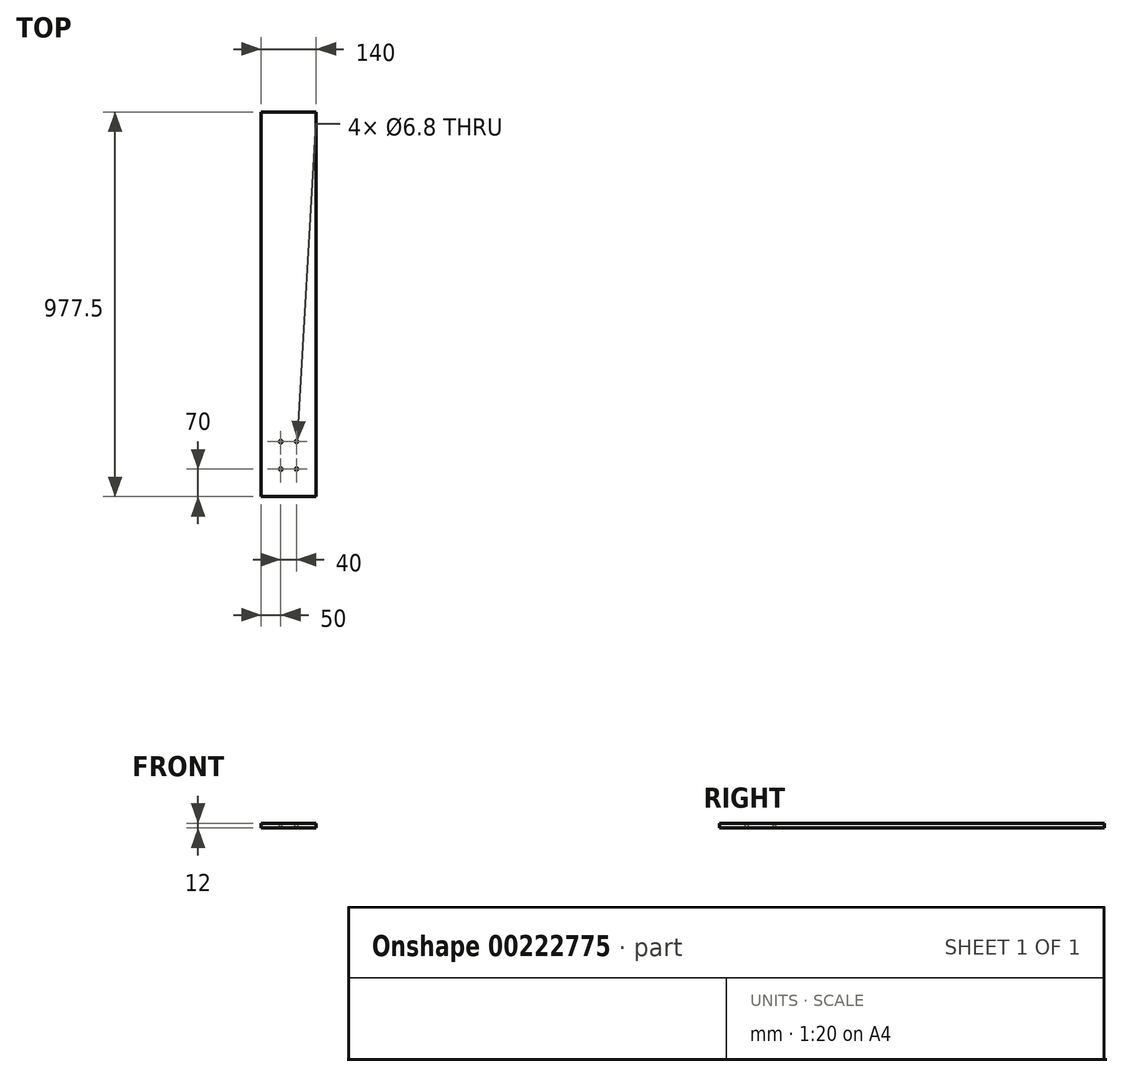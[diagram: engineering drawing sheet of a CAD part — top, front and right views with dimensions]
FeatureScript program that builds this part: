
annotation { "Feature Type Name" : "Feature", "Feature Type Description" : "" }
export const myFeature = defineFeature(function(context is Context, id is Id, definition is map)
    precondition{}
    {
        {
            var Q0;
            Q0=qCreatedBy(makeId("Top.planeOp"),FACE);
            var sketch = newSketch(context, id + "F0", { "sketchPlane" : qUnion([Q0])});
            skLineSegment(sketch, "E0.bottom", {"start": v(0, 0) * mm, "end": v(140, 0) * mm});
            skLineSegment(sketch, "E0.top", {"start": v(0, 977.5) * mm, "end": v(140, 977.5) * mm});
            skLineSegment(sketch, "E0.left", {"start": v(0, 0) * mm, "end": v(0, 977.5) * mm});
            skLineSegment(sketch, "E0.right", {"start": v(140, 0) * mm, "end": v(140, 977.5) * mm});
            skSolve(sketch);
        }
        {
            var Q0;
            Q0 = qSketchRegion(id + "F0", true);
            extrude(context, id + "F1", {"entities" : qUnion([Q0]), "depth" : 12 * mm});
        }
        {
            var Q0;
            Q0=makeQuery(id+"F1.opExtrude","CAP_FACE",FACE,{"disambiguationData":[OSD([sQuery(id+"F0.wireOp",EDGE,"E0.bottom"),sQuery(id+"F0.wireOp",EDGE,"E0.top"),sQuery(id+"F0.wireOp",EDGE,"E0.left"),sQuery(id+"F0.wireOp",EDGE,"E0.right")])],"isStart":false});
            var sketch = newSketch(context, id + "F2", { "sketchPlane" : qUnion([Q0])});
            skLineSegment(sketch, "E1.bottom", {"start": v(50, 70) * mm, "end": v(90, 70) * mm});
            skLineSegment(sketch, "E1.top", {"start": v(50, 140) * mm, "end": v(90, 140) * mm});
            skLineSegment(sketch, "E1.left", {"start": v(50, 70) * mm, "end": v(50, 140) * mm});
            skLineSegment(sketch, "E1.right", {"start": v(90, 70) * mm, "end": v(90, 140) * mm});
            skLineSegment(sketch, "E2", {"start": v(70, 0) * mm, "end": v(70, 240.08) * mm, "construction": true});
            skSolve(sketch);
        }
        {
            var Q0;
            Q0=sQuery(id+"F2.wireOp",VERTEX,"E1.left.end");
            var Q1;
            Q1=sQuery(id+"F2.wireOp",VERTEX,"E1.top.end");
            var Q2;
            Q2=sQuery(id+"F2.wireOp",VERTEX,"E1.right.start");
            var Q3;
            Q3=sQuery(id+"F2.wireOp",VERTEX,"E1.left.start");
            var Q4;
            Q4=makeQuery(id+"F1.opExtrude","SWEPT_BODY",BODY,{"disambiguationData":[OSD([sQuery(id+"F0.wireOp",EDGE,"E0.bottom"),sQuery(id+"F0.wireOp",EDGE,"E0.top"),sQuery(id+"F0.wireOp",EDGE,"E0.left"),sQuery(id+"F0.wireOp",EDGE,"E0.right")])]});
            hole(context, id + "F3", {"style" : HoleStyle.SIMPLE, "endStyle" : HoleEndStyle.THROUGH, "standardTappedOrClearance" : lookupTablePath({ "standard" : "ISO", "engagement" : "75%", "pitch" : "1.25 mm", "size" : "M8", "type" : "Tapped" }), "standardBlindInLast" : lookupTablePath({ "standard" : "ISO", "engagement" : "75%", "pitch" : "1.25 mm", "size" : "M8", "type" : "Tapped" }), "holeDiameter" : 6.8 * mm, "showTappedDepth" : true, "isTappedThrough" : true, "tappedDepth" : 12 * mm, "tapClearance" : 3, "locations" : qUnion([Q0, Q1, Q2, Q3]), "scope" : qUnion([Q4]), "majorDiameter" : 8 * mm});
        }
    });
